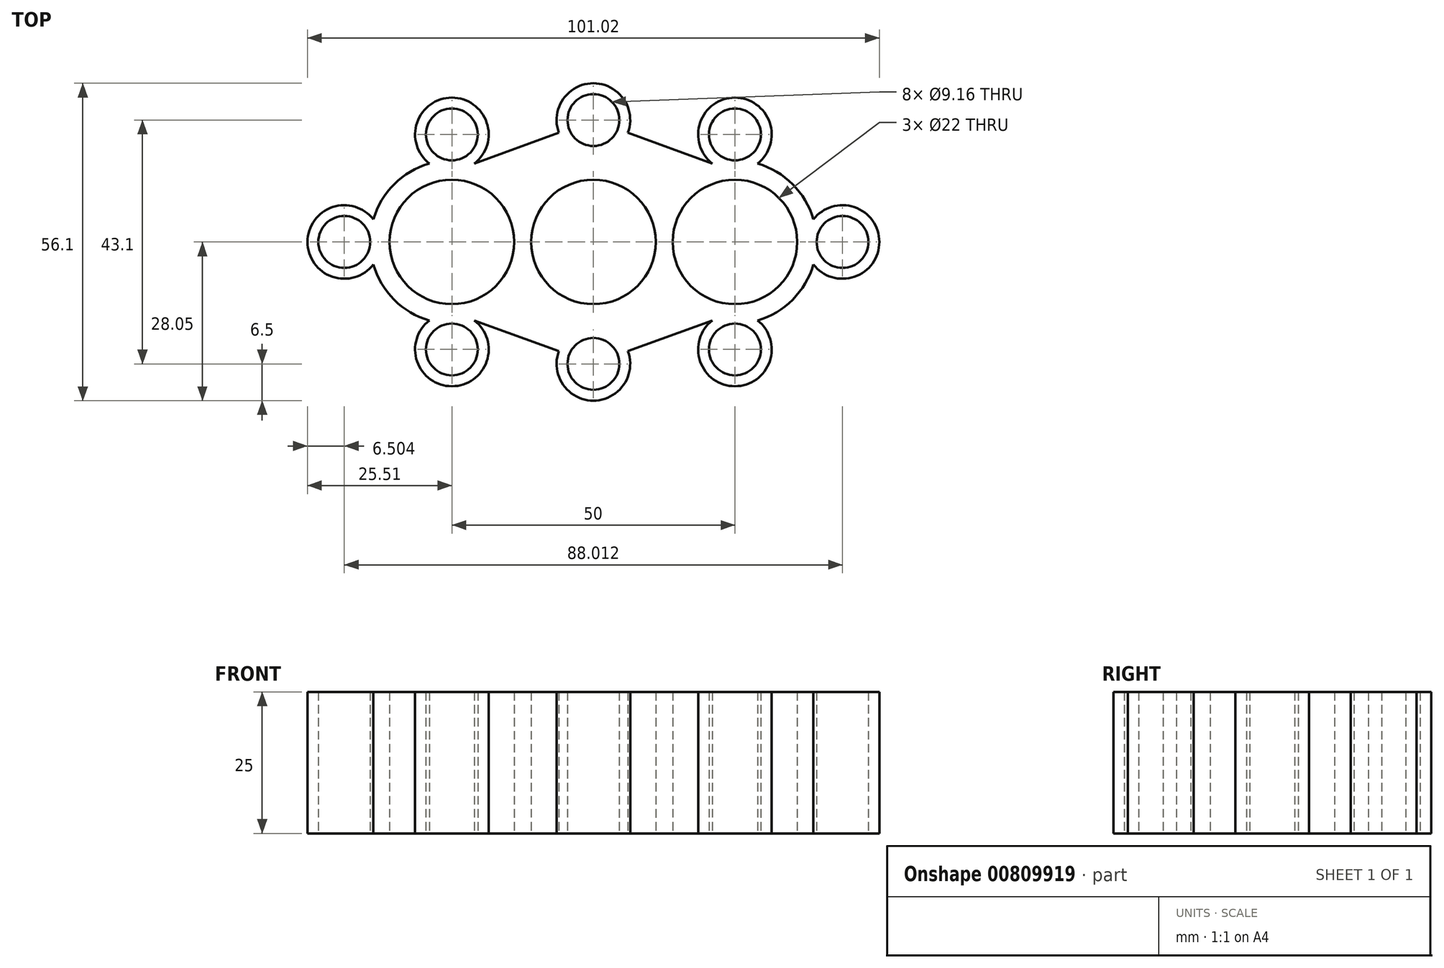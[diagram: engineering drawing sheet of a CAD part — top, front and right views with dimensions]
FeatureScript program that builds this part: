
annotation { "Feature Type Name" : "Feature", "Feature Type Description" : "" }
export const myFeature = defineFeature(function(context is Context, id is Id, definition is map)
    precondition{}
    {
        {
            var Q0;
            Q0=qCreatedBy(makeId("Top.planeOp"),FACE);
            var sketch = newSketch(context, id + "F0", { "sketchPlane" : qUnion([Q0])});
            skArc(sketch, "E0", {"start": v(0, 11) * mm, "mid": v(-11, 0) * mm, "end": v(0, -11) * mm});
            skArc(sketch, "E1", {"start": v(-14.58, 3.52) * mm, "mid": v(-36, 0) * mm, "end": v(-14.58, -3.52) * mm});
            skArc(sketch, "E2", {"start": v(-14.58, -3.52) * mm, "mid": v(-14, 0) * mm, "end": v(-14.58, 3.52) * mm});
            skLineSegment(sketch, "E3", {"start": v(0, -11) * mm, "end": v(0, -15) * mm});
            skPoint(sketch, "E4.orphan", {"position": v(0, 21.55) * mm});
            skArc(sketch, "E5.MirrorCS", {"start": v(14.58, 3.52) * mm, "mid": v(36, 0) * mm, "end": v(14.58, -3.52) * mm});
            skArc(sketch, "E6.MirrorCS", {"start": v(14.58, -3.52) * mm, "mid": v(14, 0) * mm, "end": v(14.58, 3.52) * mm});
            skArc(sketch, "E7.MirrorCS", {"start": v(0, 11) * mm, "mid": v(11, 0) * mm, "end": v(0, -11) * mm});
            skArc(sketch, "E8", {"start": v(-38.87, 3.98) * mm, "mid": v(-50.5, 0) * mm, "end": v(-38.87, -3.98) * mm});
            skCircle(sketch, "E9", {"center": v(-44, 0) * mm, "radius": 4.58 * mm});
            skArc(sketch, "E10.trimOffspring", {"start": v(-38.87, -3.98) * mm, "mid": v(-35.2, -10.2) * mm, "end": v(-28.98, -13.87) * mm});
            skArc(sketch, "E11", {"start": v(38.87, -3.98) * mm, "mid": v(50.5, 0) * mm, "end": v(38.87, 3.98) * mm});
            skCircle(sketch, "E12", {"center": v(44, 0) * mm, "radius": 4.58 * mm});
            skArc(sketch, "E13.trimOffspring", {"start": v(38.87, -3.98) * mm, "mid": v(35.2, -10.2) * mm, "end": v(28.98, -13.87) * mm});
            skLineSegment(sketch, "E14", {"start": v(-25, 0) * mm, "end": v(-25, 19) * mm});
            skArc(sketch, "E15", {"start": v(-21.02, 13.87) * mm, "mid": v(-25, 25.5) * mm, "end": v(-28.98, 13.87) * mm});
            skCircle(sketch, "E16", {"center": v(-25, 19) * mm, "radius": 4.58 * mm});
            skLineSegment(sketch, "E17", {"start": v(-25, 0) * mm, "end": v(-25, -19) * mm});
            skArc(sketch, "E18", {"start": v(-28.98, -13.87) * mm, "mid": v(-25, -25.5) * mm, "end": v(-21.02, -13.87) * mm});
            skCircle(sketch, "E19", {"center": v(-25, -19) * mm, "radius": 4.58 * mm});
            skLineSegment(sketch, "E20", {"start": v(25, 0) * mm, "end": v(25, 19) * mm});
            skArc(sketch, "E21", {"start": v(28.98, 13.87) * mm, "mid": v(25, 25.5) * mm, "end": v(21.02, 13.87) * mm});
            skCircle(sketch, "E22", {"center": v(25, 19) * mm, "radius": 4.58 * mm});
            skLineSegment(sketch, "E23", {"start": v(25, 0) * mm, "end": v(25, -19) * mm});
            skArc(sketch, "E24", {"start": v(21.02, -13.87) * mm, "mid": v(25, -25.5) * mm, "end": v(28.98, -13.87) * mm});
            skCircle(sketch, "E25", {"center": v(25, -19) * mm, "radius": 4.58 * mm});
            skArc(sketch, "E26.trimOffspring", {"start": v(-28.98, 13.87) * mm, "mid": v(-35.2, 10.2) * mm, "end": v(-38.87, 3.98) * mm});
            skArc(sketch, "E27.trimOffspring", {"start": v(28.98, 13.87) * mm, "mid": v(35.2, 10.2) * mm, "end": v(38.87, 3.98) * mm});
            skLineSegment(sketch, "E28", {"start": v(0, 0) * mm, "end": v(0, -11) * mm});
            skLineSegment(sketch, "E29", {"start": v(-21.02, -13.87) * mm, "end": v(-6.1, -19.32) * mm});
            skLineSegment(sketch, "E30", {"start": v(6.1, -19.32) * mm, "end": v(21.02, -13.87) * mm});
            skLineSegment(sketch, "E31", {"start": v(-21.02, 13.87) * mm, "end": v(-6.1, 19.32) * mm});
            skLineSegment(sketch, "E32", {"start": v(6.1, 19.32) * mm, "end": v(21.02, 13.87) * mm});
            skPoint(sketch, "E33.trimOffspring.end.orphan", {"position": v(-12.84, 7.76) * mm});
            skPoint(sketch, "E33.trimOffspring.start.orphan", {"position": v(0, 15.05) * mm});
            skPoint(sketch, "E34.MirrorCS.end.orphan", {"position": v(12.84, 7.76) * mm});
            skPoint(sketch, "E35.MirrorCS.end.orphan", {"position": v(0, -15) * mm});
            skPoint(sketch, "E35.MirrorCS.start.orphan", {"position": v(12.84, -7.76) * mm});
            skPoint(sketch, "E36.trimOffspring.end.orphan", {"position": v(-12.84, -7.76) * mm});
            skLineSegment(sketch, "E37.trimOffspring", {"start": v(0, -15) * mm, "end": v(0, -21.55) * mm});
            skLineSegment(sketch, "E38.trimOffspring", {"start": v(0, 11) * mm, "end": v(0, 0) * mm});
            skArc(sketch, "E39", {"start": v(6.1, 19.32) * mm, "mid": v(0, 28.05) * mm, "end": v(-6.1, 19.32) * mm});
            skCircle(sketch, "E40", {"center": v(0, 21.55) * mm, "radius": 4.58 * mm});
            skArc(sketch, "E41", {"start": v(-6.1, -19.32) * mm, "mid": v(0, -28.05) * mm, "end": v(6.1, -19.32) * mm});
            skCircle(sketch, "E42", {"center": v(0, -21.55) * mm, "radius": 4.58 * mm});
            skSolve(sketch);
        }
        {
            var Q0;
            Q0 = qSketchRegion(id + "F0", true);
            extrude(context, id + "F1", {"entities" : qUnion([Q0]), "depth" : 25 * mm, "offsetDistance" : 25 * mm});
        }
    });
